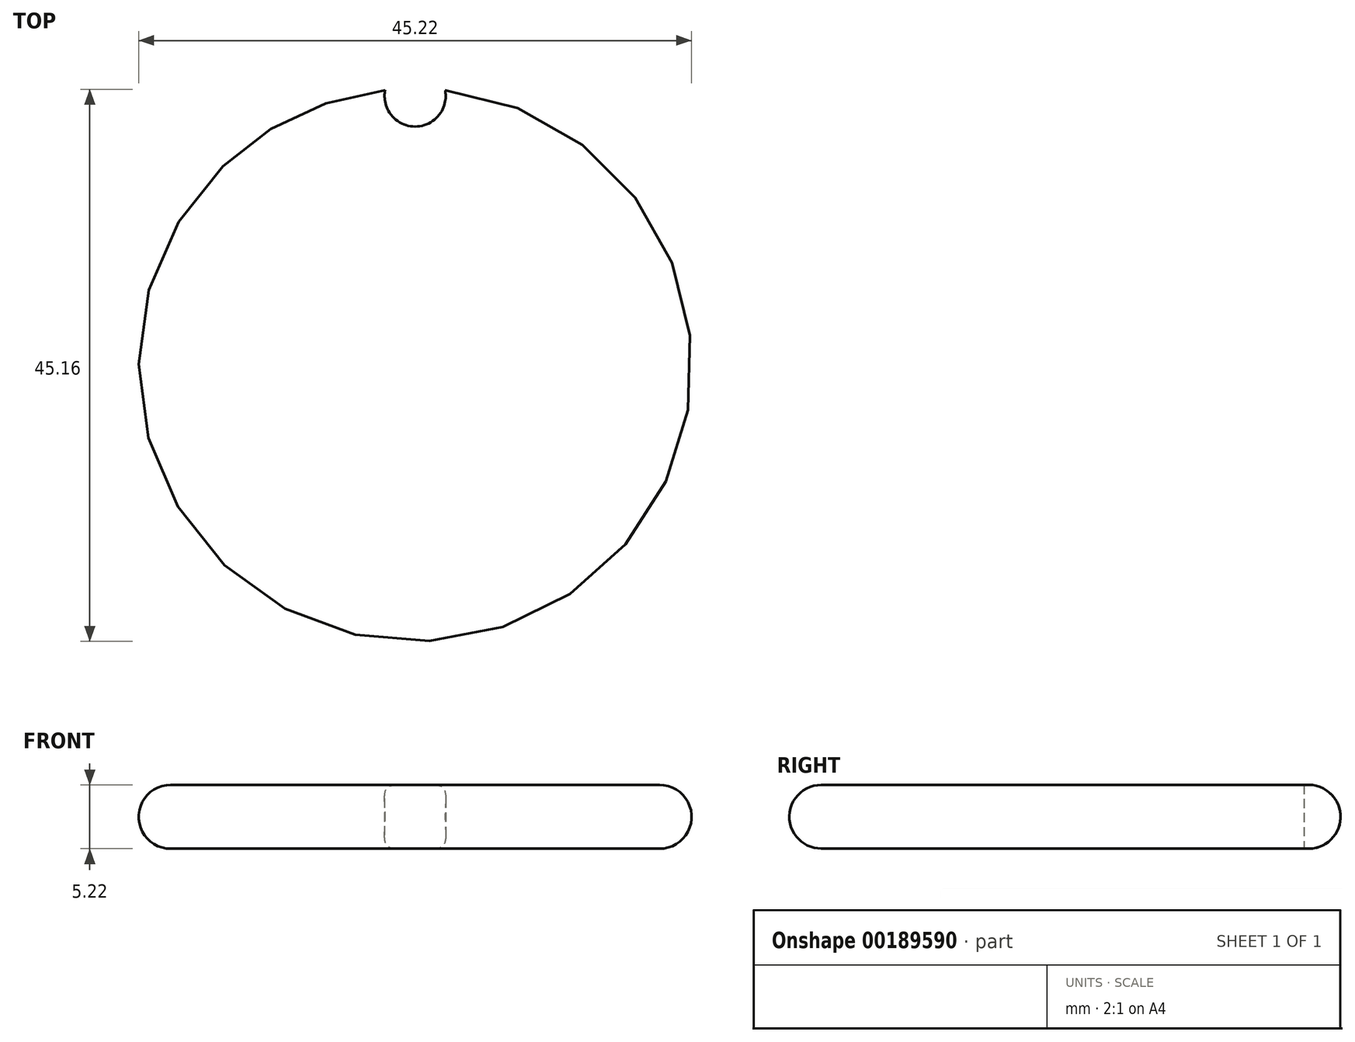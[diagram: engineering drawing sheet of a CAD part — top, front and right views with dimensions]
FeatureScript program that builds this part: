
annotation { "Feature Type Name" : "Feature", "Feature Type Description" : "" }
export const myFeature = defineFeature(function(context is Context, id is Id, definition is map)
    precondition{}
    {
        {
            var Q0;
            Q0=qCreatedBy(makeId("Front.planeOp"),FACE);
            var sketch = newSketch(context, id + "F0", { "sketchPlane" : qUnion([Q0])});
            skLineSegment(sketch, "E0.bottom", {"start": v(0, 0) * mm, "end": v(-20, 0) * mm});
            skLineSegment(sketch, "E0.top", {"start": v(0, 5.22) * mm, "end": v(-20, 5.22) * mm});
            skLineSegment(sketch, "E0.left", {"start": v(0, 0) * mm, "end": v(0, 5.22) * mm});
            skLineSegment(sketch, "E0.right", {"start": v(-20, 0) * mm, "end": v(-20, 5.22) * mm});
            skArc(sketch, "E1", {"start": v(-20, 5.22) * mm, "mid": v(-22.61, 2.61) * mm, "end": v(-20, 0) * mm});
            skSolve(sketch);
        }
        {
            var Q0;
            Q0 = qSketchRegion(id + "F0", true);
            var Q1;
            Q1=sQuery(id+"F0.wireOp",EDGE,"E0.left");
            revolve(context, id + "F1", {"entities" : qUnion([Q0]), "axis" : qUnion([Q1]), "revolveType" : RevolveType.FULL});
        }
        {
            var Q0;
            Q0=qCreatedBy(makeId("Top.planeOp"),FACE);
            var sketch = newSketch(context, id + "F2", { "sketchPlane" : qUnion([Q0])});
            skCircle(sketch, "E2", {"center": v(0, 22) * mm, "radius": 2.5 * mm});
            skSolve(sketch);
        }
        {
            var Q0;
            Q0 = qSketchRegion(id + "F2", true);
            extrude(context, id + "F3", {"entities" : qUnion([Q0]), "operationType" : NewBodyOperationType.REMOVE, "depth" : 25.4 * mm});
        }
    });
